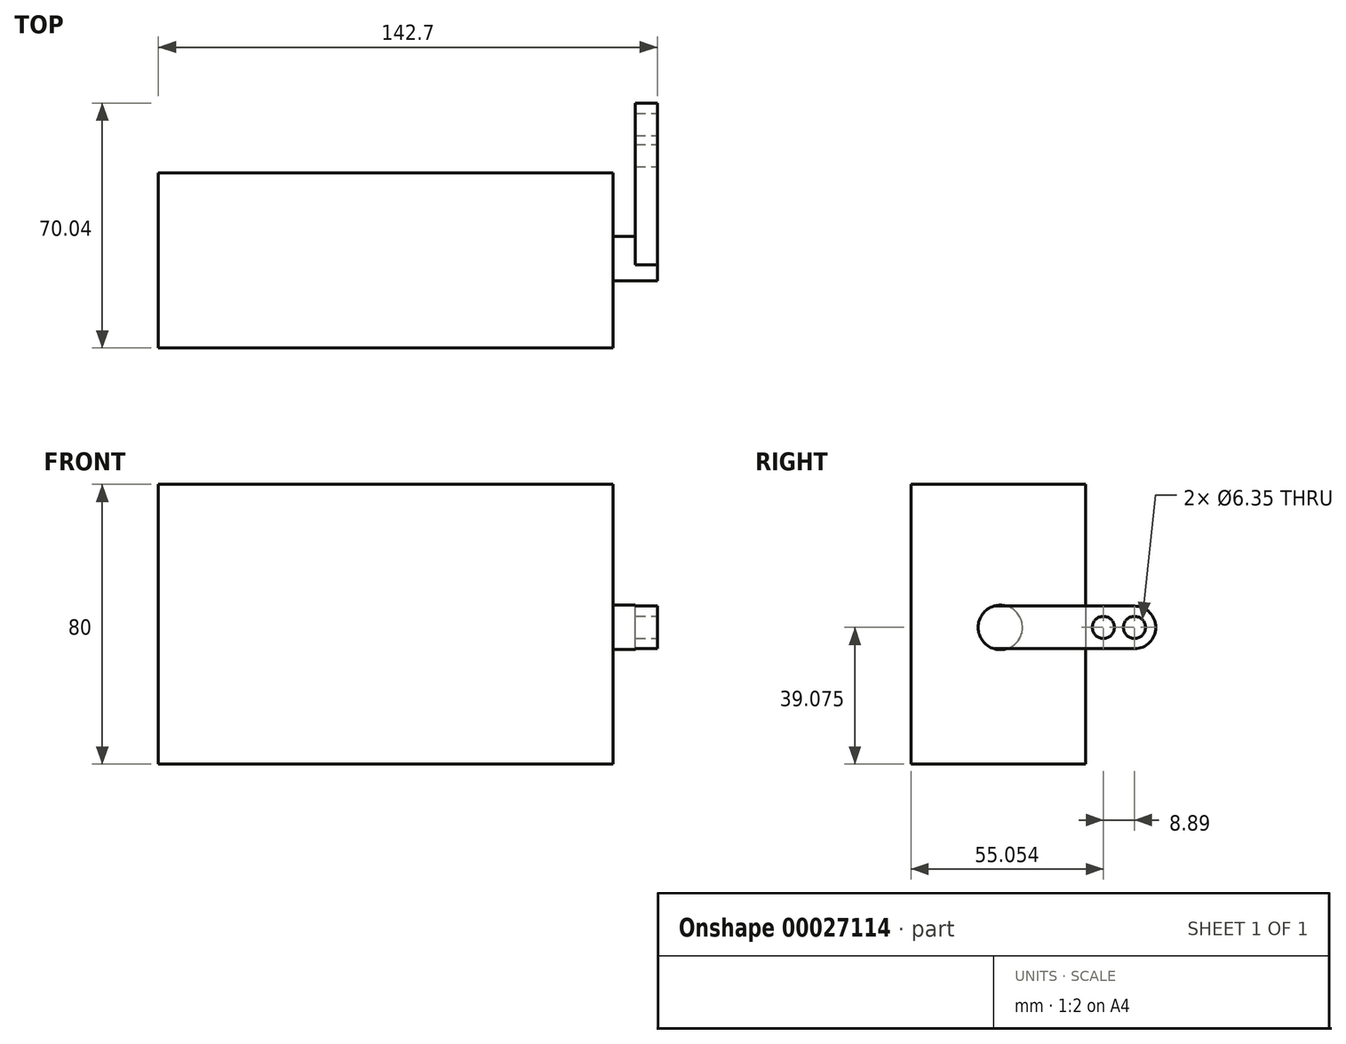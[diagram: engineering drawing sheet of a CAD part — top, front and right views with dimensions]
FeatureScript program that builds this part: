
annotation { "Feature Type Name" : "Feature", "Feature Type Description" : "" }
export const myFeature = defineFeature(function(context is Context, id is Id, definition is map)
    precondition{}
    {
        {
            var Q0;
            Q0=qCreatedBy(makeId("Front.planeOp"),FACE);
            var sketch = newSketch(context, id + "F0", { "sketchPlane" : qUnion([Q0])});
            skLineSegment(sketch, "E0.bottom", {"start": v(-4.1, 88.8) * mm, "end": v(125.9, 88.8) * mm});
            skLineSegment(sketch, "E0.top", {"start": v(-4.1, 8.8) * mm, "end": v(125.9, 8.8) * mm});
            skLineSegment(sketch, "E0.left", {"start": v(-4.1, 88.8) * mm, "end": v(-4.1, 8.8) * mm});
            skLineSegment(sketch, "E0.right", {"start": v(125.9, 88.8) * mm, "end": v(125.9, 8.8) * mm});
            skSolve(sketch);
        }
        {
            var Q0;
            Q0=makeQuery(id+"F0.imprint","IMPRINT",FACE,{"disambiguationData":[TD([[makeQuery(id+"F0.imprint","IMPRINT",EDGE,{"derivedFrom":sQuery(id+"F0.wireOp",EDGE,"E0.bottom")}),-1.0]])]});
            extrude(context, id + "F1", {"entities" : qUnion([Q0]), "depth" : 50 * mm});
        }
        {
            var Q0;
            Q0=makeQuery(id+"F1.opExtrude","SWEPT_FACE",FACE,{"disambiguationData":[OSD([sQuery(id+"F0.wireOp",EDGE,"E0.right")])]});
            var sketch = newSketch(context, id + "F2", { "sketchPlane" : qUnion([Q0])});
            skCircle(sketch, "E1", {"center": v(-24.4, 47.89) * mm, "radius": 6.35 * mm});
            skSolve(sketch);
        }
        {
            var Q0;
            Q0=makeQuery(id+"F2.imprint","IMPRINT",FACE,{"disambiguationData":[TD([[makeQuery(id+"F2.imprint","IMPRINT",EDGE,{"derivedFrom":sQuery(id+"F2.wireOp",EDGE,"E1")}),1.0]])]});
            extrude(context, id + "F3", {"entities" : qUnion([Q0]), "operationType" : NewBodyOperationType.ADD, "depth" : 6.35 * mm});
        }
        {
            var Q0;
            Q0=makeQuery(id+"F3.opExtrude","CAP_FACE",FACE,{"disambiguationData":[OSD([sQuery(id+"F2.wireOp",EDGE,"E1")])],"isStart":false});
            var sketch = newSketch(context, id + "F4", { "sketchPlane" : qUnion([Q0])});
            skLineSegment(sketch, "E2", {"start": v(-26.18, 53.98) * mm, "end": v(13.94, 53.98) * mm});
            skLineSegment(sketch, "E3", {"start": v(-26.18, 41.79) * mm, "end": v(13.94, 41.79) * mm});
            skArc(sketch, "E4", {"start": v(-22.64, 53.98) * mm, "mid": v(-30.76, 47.89) * mm, "end": v(-22.64, 41.79) * mm});
            skArc(sketch, "E5", {"start": v(13.94, 41.79) * mm, "mid": v(20.04, 47.89) * mm, "end": v(13.94, 53.98) * mm});
            skSolve(sketch);
        }
        {
            var Q0;
            {var subQ6=sQuery(id+"F4.wireOp",EDGE,"E5");Q0=makeQuery(id+"F4.imprint","IMPRINT",FACE,{"disambiguationData":[TD([[makeQuery(id+"F4.imprint","IMPRINT",EDGE,{"derivedFrom":subQ6}),1.0]])]});}
            var Q1;
            {var subQ2=sQuery(id+"F4.wireOp",EDGE,"E4");var subQ4=sQuery(id+"F4.wireOp",EDGE,"E2");var subQ7=makeQuery(id+"F4.imprint","INTERSECT",VERTEX,{"derivedFrom":[subQ4,subQ2]});Q1=makeQuery(id+"F4.imprint","IMPRINT",FACE,{"disambiguationData":[TD([[makeQuery(id+"F4.imprint","IMPRINT",EDGE,{"disambiguationData":[TD([[subQ7,-1.0]])],"derivedFrom":subQ2}),1.0]])]});}
            extrude(context, id + "F5", {"entities" : qUnion([Q0, Q1]), "operationType" : NewBodyOperationType.ADD, "depth" : 6.35 * mm});
        }
        {
            var Q0;
            Q0=makeQuery(id+"F5.opExtrude","CAP_FACE",FACE,{"disambiguationData":[OSD([sQuery(id+"F4.wireOp",EDGE,"E2"),sQuery(id+"F4.wireOp",EDGE,"E3"),sQuery(id+"F4.wireOp",EDGE,"E4"),sQuery(id+"F4.wireOp",EDGE,"E5")])],"isStart":false});
            var sketch = newSketch(context, id + "F6", { "sketchPlane" : qUnion([Q0])});
            skCircle(sketch, "E6", {"center": v(13.94, 47.89) * mm, "radius": 3.18 * mm});
            skCircle(sketch, "E7", {"center": v(5.05, 47.89) * mm, "radius": 3.18 * mm});
            skSolve(sketch);
        }
        {
            var Q0;
            Q0=makeQuery(id+"F6.imprint","IMPRINT",FACE,{"disambiguationData":[TD([[makeQuery(id+"F6.imprint","IMPRINT",EDGE,{"derivedFrom":sQuery(id+"F6.wireOp",EDGE,"E7")}),1.0]])]});
            var Q1;
            Q1=makeQuery(id+"F6.imprint","IMPRINT",FACE,{"disambiguationData":[TD([[makeQuery(id+"F6.imprint","IMPRINT",EDGE,{"derivedFrom":sQuery(id+"F6.wireOp",EDGE,"E6")}),1.0]])]});
            extrude(context, id + "F7", {"entities" : qUnion([Q0, Q1]), "operationType" : NewBodyOperationType.REMOVE, "endBound" : BoundingType.THROUGH_ALL, "oppositeDirection" : true, "depth" : 25.4 * mm});
        }
    });
